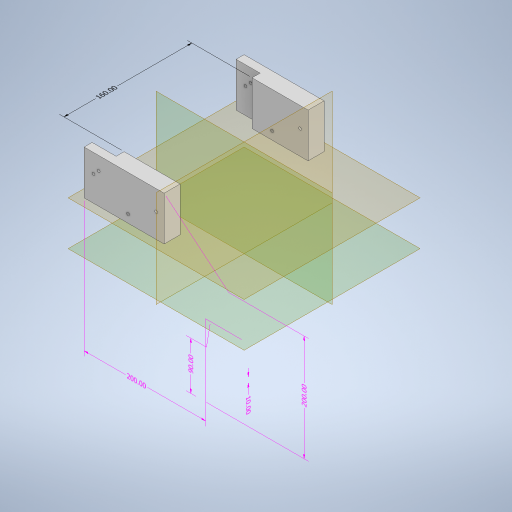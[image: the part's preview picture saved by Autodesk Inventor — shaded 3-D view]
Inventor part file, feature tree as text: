
AUTODESK INVENTOR PART (.ipt)
format: ipt  version: 2023 (Build 270158000, 158)  size: 449,536 bytes
history: native  units: mm
features: sketch x9, other x8, extrude x5, hole x4, plane x4, split x3
ambient origin geometry x8: Origin, YZ Plane, XZ Plane, XY Plane, X Axis, Y Axis, Z Axis, Center Point
bodies: Body1 (feature_tree)
feature tree (33):
  other  "Sólido1"
  other  "Anotaciones"
  extrude  "Extrusión1"  Depth=200.0mm
  hole  "Agujero1"  [1 undecoded]
  extrude  "Extrusión2"  Depth=15.0mm
  extrude  "Extrusión3"  Depth=20.0mm TaperAngle=0.0deg
  extrude  "Extrusión4"  Depth=200.0mm
  extrude  "Extrusión5"  Depth=20.0mm
  hole  "Agujero2"  [1 undecoded]
  plane  "Plano de trabajo1"
  split  "Dividir1"
  plane  "Plano de trabajo2"
  plane  "Plano de trabajo3"
  plane  "Plano de trabajo4"
  hole  "Agujero3"  [1 undecoded]
  hole  "Agujero4"  [1 undecoded]
  split  "Dividir2"
  split  "Dividir3"
  sketch  "Boceto2"  dims[d7=15.0mm d8=200.0mm]
  sketch  "Boceto3"  dims[d9=10.0mm d10=0.0mm]
  sketch  "Boceto4"  dims[d11=3.5mm d12=1.75mm d13=1.75mm d14=1.75mm d15=1.75mm d16=10.0mm d17=10.0mm d19=40.0mm]
  sketch  "Boceto5"  dims[d20=3.5mm d21=6.0mm d22=4.0mm d23=2.0mm d24=90.0deg d25=8.0mm d26=20.594885mm d27=15.0mm]
  sketch  "Boceto6"  dims[d28=20.0mm d29=80.0mm d30=0.0mm]
  sketch  "Boceto7"  dims[d31=57.0mm d32=200.0mm]
  sketch  "Boceto8"  dims[d33=110.0mm d34=0.0mm d36=20.0mm]
  sketch  "Boceto9"  dims[d37=20.0mm d38=20.0mm]
  sketch  "Boceto10"  dims[d39=90.0mm d40=0.0mm d43=30.0mm d44=0.0mm d45=3.5mm d46=1.75mm d47=1.75mm d48=1.75mm d49=1.75mm d50=10.0mm d51=10.0mm d52=15.0mm d53=10.0mm d54=10.0mm d55=15.0mm d56=3.5mm d57=6.0mm d58=4.0mm d59=2.0mm d60=90.0deg d61=8.0mm d62=20.594885mm d63=10.0mm d65=10.0mm d75=200.0mm d76=10.0mm d77=20.0mm d81=40.0mm d88=90.0deg d89=10.0mm d90=30.0mm d91=5.0mm d92=5.0mm d93=5.0mm d94=5.0mm d95=30.0mm d96=5.0mm d97=5.0mm d98=3.5mm d99=5.0mm d100=5.0mm d101=5.0mm d102=5.0mm d103=5.0mm d104=20.0mm d105=3.5mm d106=6.0mm d107=4.0mm d108=2.0mm d109=90.0deg d110=8.0mm d111=20.594885mm d112=10.0mm d113=30.0mm d114=5.0mm d115=5.0mm d116=5.0mm d117=5.0mm d118=5.0mm d119=5.0mm d120=3.5mm d121=5.0mm d122=5.0mm d123=5.0mm d124=5.0mm d125=5.0mm d126=30.0mm d127=30.0mm d128=3.5mm d129=6.0mm d130=4.0mm d131=2.0mm d132=90.0deg d133=8.0mm d134=20.594885mm d66=5.760865mm d67=7.72461mm d68=200.0mm d69=3.008686mm d70=2.422102mm d71=10.0mm d72=3.500509mm d73=2.402572mm d74=90.0mm d78=3.13122mm d79=6.269346mm d80=200.0mm d82=8.450127mm d83=0.968417mm d84=20.0mm d85=4.759975mm d86=4.646891mm d87=160.0mm]
  other  "Cota lineal 1"
  other  "Cota lineal 2"
  other  "Cota lineal 3"
  other  "Cota lineal 4"
  other  "Cota lineal 5"
  other  "Cota lineal 6"
note: 4 required parameter values undecoded (feature->parameter linkage not recoverable at this tier; creation-order binding heuristic only, values carry confidence <= 0.55)
